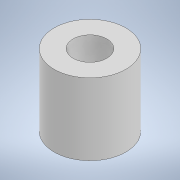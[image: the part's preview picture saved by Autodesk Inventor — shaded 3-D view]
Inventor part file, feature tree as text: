
AUTODESK INVENTOR PART (.ipt)
format: ipt  version: 2021 (Build 250183000, 183)  size: 230,400 bytes
history: native  units: mm
features: revolve x1, sketch x1
ambient origin geometry x8: Origin, YZ Plane, XZ Plane, XY Plane, X Axis, Y Axis, Z Axis, Center Point
bodies: Volumenkörper1 (feature_tree)
feature tree (2):
  revolve  "Umdrehung1"
  sketch  "Skizze1"  dims[d0=90.0deg d1=5.0mm d2=2.35mm d3=5.0mm d5=90.0deg]
